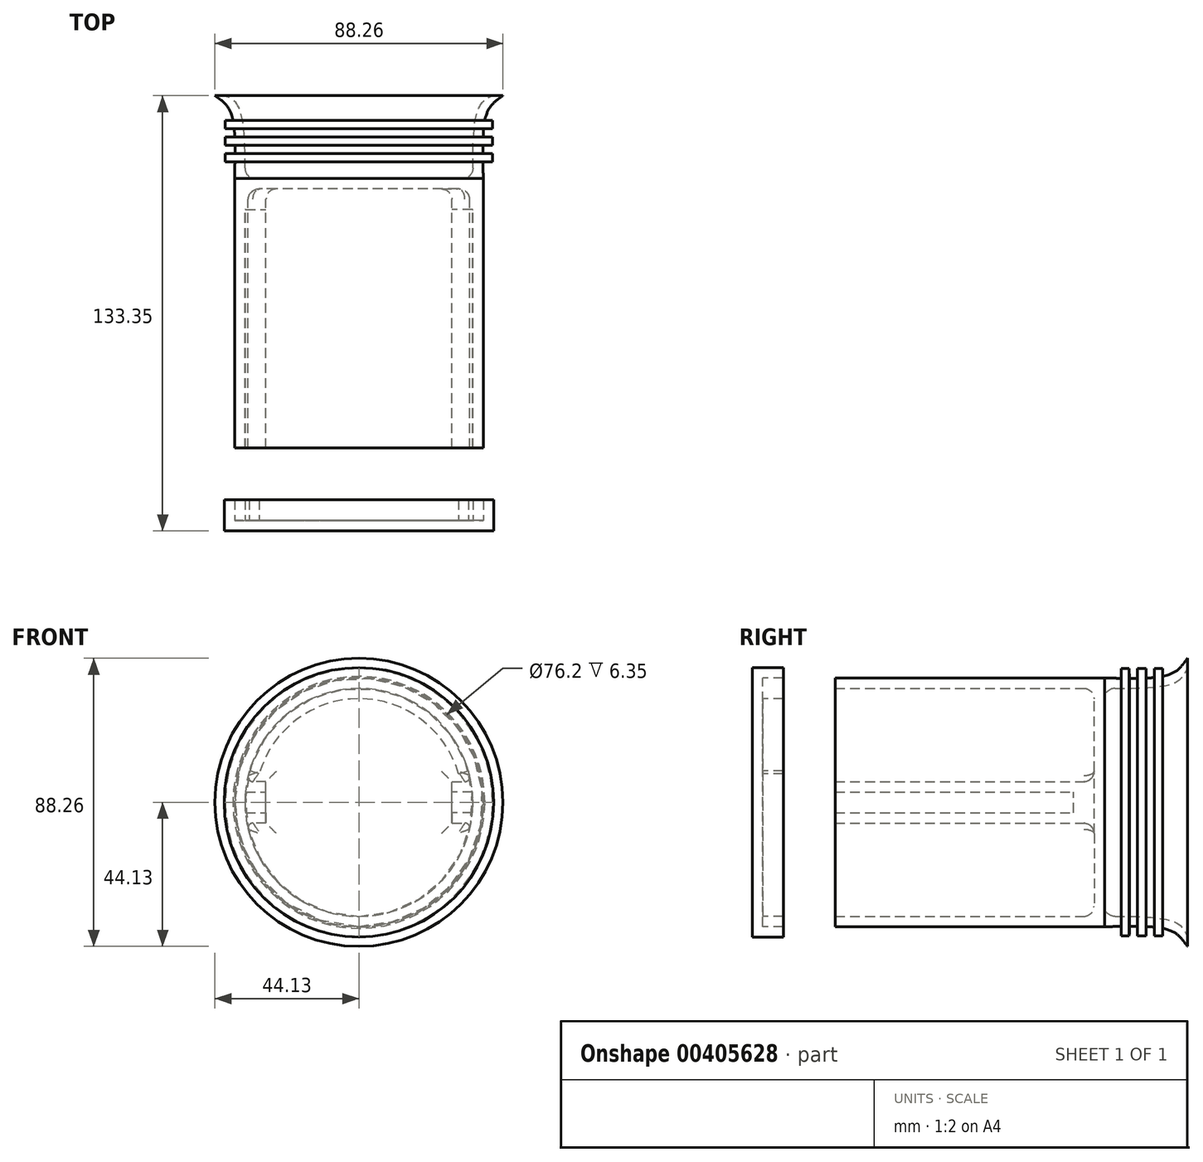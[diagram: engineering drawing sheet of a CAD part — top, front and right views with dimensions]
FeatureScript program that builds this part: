
annotation { "Feature Type Name" : "Feature", "Feature Type Description" : "" }
export const myFeature = defineFeature(function(context is Context, id is Id, definition is map)
    precondition{}
    {
        {
            var Q0;
            Q0=qCreatedBy(makeId("Front.planeOp"),FACE);
            var sketch = newSketch(context, id + "F0", { "sketchPlane" : qUnion([Q0])});
            skCircle(sketch, "E0", {"center": v(0, 0) * mm, "radius": 34.93 * mm});
            skCircle(sketch, "E1", {"center": v(0, 0) * mm, "radius": 38.1 * mm});
            skPoint(sketch, "E2", {"position": v(-38.1, 0) * mm});
            skPoint(sketch, "E3", {"position": v(38.1, 0) * mm});
            skPoint(sketch, "E4", {"position": v(-34.93, 0) * mm});
            skPoint(sketch, "E5", {"position": v(34.93, 0) * mm});
            skLineSegment(sketch, "E6", {"start": v(-38.1, 0) * mm, "end": v(38.1, 0) * mm, "construction": true});
            skLineSegment(sketch, "E7", {"start": v(34.78, -3.17) * mm, "end": v(28.48, -3.17) * mm});
            skLineSegment(sketch, "E8", {"start": v(28.48, -3.17) * mm, "end": v(28.48, -6.35) * mm});
            skLineSegment(sketch, "E9", {"start": v(28.48, -6.35) * mm, "end": v(34.34, -6.35) * mm});
            skLineSegment(sketch, "E10.MirrorCS", {"start": v(28.48, 3.17) * mm, "end": v(28.48, 6.35) * mm});
            skLineSegment(sketch, "E11.MirrorCS", {"start": v(28.48, 6.35) * mm, "end": v(34.34, 6.35) * mm});
            skLineSegment(sketch, "E12.MirrorCS", {"start": v(34.78, 3.17) * mm, "end": v(28.48, 3.17) * mm});
            skLineSegment(sketch, "E13.MirrorCS", {"start": v(-34.78, -3.17) * mm, "end": v(-28.48, -3.17) * mm});
            skLineSegment(sketch, "E14.MirrorCS", {"start": v(-28.48, 3.17) * mm, "end": v(-28.48, 6.35) * mm});
            skLineSegment(sketch, "E15.MirrorCS", {"start": v(-34.78, 3.17) * mm, "end": v(-28.48, 3.17) * mm});
            skLineSegment(sketch, "E16.MirrorCS", {"start": v(-28.48, -3.17) * mm, "end": v(-28.48, -6.35) * mm});
            skLineSegment(sketch, "E17.MirrorCS", {"start": v(-28.48, -6.35) * mm, "end": v(-34.34, -6.35) * mm});
            skLineSegment(sketch, "E18.MirrorCS", {"start": v(-28.48, 6.35) * mm, "end": v(-34.34, 6.35) * mm});
            skLineSegment(sketch, "E19", {"start": v(28.48, -3.17) * mm, "end": v(28.48, 3.17) * mm});
            skLineSegment(sketch, "E20", {"start": v(-28.48, -3.17) * mm, "end": v(-28.48, 3.17) * mm});
            skSolve(sketch);
        }
        {
            var Q0;
            Q0=makeQuery(id+"F0.imprint","IMPRINT",FACE,{"disambiguationData":[TD([[makeQuery(id+"F0.imprint","IMPRINT",EDGE,{"derivedFrom":sQuery(id+"F0.wireOp",EDGE,"E1")}),1.0]])]});
            var Q1;
            {var subQ0=sQuery(id+"F0.wireOp",EDGE,"b258979f-0020-4e8b-a2a5-557b5379ad452.MirrorCS");Q1=makeQuery(id+"F0.imprint","IMPRINT",FACE,{"disambiguationData":[TD([[makeQuery(id+"F0.imprint","IMPRINT",EDGE,{"derivedFrom":subQ0}),-1.0]])]});}
            var Q2;
            {var subQ0=sQuery(id+"F0.wireOp",EDGE,"b258979f-0020-4e8b-a2a5-557b5379ad450.MirrorCS");Q2=makeQuery(id+"F0.imprint","IMPRINT",FACE,{"disambiguationData":[TD([[makeQuery(id+"F0.imprint","IMPRINT",EDGE,{"derivedFrom":subQ0}),1.0]])]});}
            var Q3;
            {var subQ0=sQuery(id+"F0.wireOp",EDGE,"MPTAMjUX-TAAp-zu8y-YZ0W-t5zbDO9KEc0N");Q3=makeQuery(id+"F0.imprint","IMPRINT",FACE,{"disambiguationData":[TD([[makeQuery(id+"F0.imprint","IMPRINT",EDGE,{"derivedFrom":subQ0}),1.0]])]});}
            var Q4;
            {var subQ0=sQuery(id+"F0.wireOp",EDGE,"9249f0fd-918d-4ee5-9cbe-e812a7f5fd550.MirrorCS");Q4=makeQuery(id+"F0.imprint","IMPRINT",FACE,{"disambiguationData":[TD([[makeQuery(id+"F0.imprint","IMPRINT",EDGE,{"derivedFrom":subQ0}),-1.0]])]});}
            var Q5;
            {var subQ0=sQuery(id+"F0.wireOp",EDGE,"E13.MirrorCS");Q5=makeQuery(id+"F0.imprint","IMPRINT",FACE,{"disambiguationData":[TD([[makeQuery(id+"F0.imprint","IMPRINT",EDGE,{"derivedFrom":subQ0}),-1.0]])]});}
            var Q6;
            Q6=makeQuery(id+"F0.imprint","IMPRINT",FACE,{"disambiguationData":[TD([[makeQuery(id+"F0.imprint","IMPRINT",EDGE,{"derivedFrom":sQuery(id+"F0.wireOp",EDGE,"E14.MirrorCS")}),1.0]])]});
            var Q7;
            {var subQ0=sQuery(id+"F0.wireOp",EDGE,"E7");Q7=makeQuery(id+"F0.imprint","IMPRINT",FACE,{"disambiguationData":[TD([[makeQuery(id+"F0.imprint","IMPRINT",EDGE,{"derivedFrom":subQ0}),1.0]])]});}
            var Q8;
            Q8=makeQuery(id+"F0.imprint","IMPRINT",FACE,{"disambiguationData":[TD([[makeQuery(id+"F0.imprint","IMPRINT",EDGE,{"derivedFrom":sQuery(id+"F0.wireOp",EDGE,"E10.MirrorCS")}),-1.0]])]});
            extrude(context, id + "F1", {"entities" : qUnion([Q0, Q1, Q2, Q3, Q4, Q5, Q6, Q7, Q8]), "depth" : 82.55 * mm});
        }
        {
            var Q0;
            Q0=qCreatedBy(makeId("Front.planeOp"),FACE);
            cPlane(context, id + "F2", {"entities" : qUnion([Q0]), "cplaneType" : CPlaneType.OFFSET, "offset" : 107.95 * mm, "width" : 152.4 * mm, "height" : 152.4 * mm});
        }
        {
            var Q0;
            Q0=qCreatedBy(makeId("Top.planeOp"),FACE);
            var sketch = newSketch(context, id + "F3", { "sketchPlane" : qUnion([Q0])});
            skLineSegment(sketch, "E21", {"start": v(-38.1, 0) * mm, "end": v(-38.1, 25.4) * mm, "construction": true});
            skLineSegment(sketch, "E22", {"start": v(-41.53, 25.4) * mm, "end": v(-41.77, 25.4) * mm, "construction": true});
            skPoint(sketch, "E23", {"position": v(-40.96, 25.4) * mm});
            skFitSpline(sketch, "E24", {"points": [v(-38.1, 0) * mm, v(-39.35, 20.4) * mm, v(-44.13, 25.4) * mm], "startDerivative": vector(0.67, 36.34) * mm, "endDerivative": vector(-15.53, 10.92) * mm});
            skFitSpline(sketch, "E25", {"points": [v(-34.93, 0) * mm, v(-36.6, 21.36) * mm, v(-40.96, 25.4) * mm], "startDerivative": vector(0.3, 37.48) * mm, "endDerivative": vector(-17.18, 7.87) * mm});
            skLineSegment(sketch, "E26", {"start": v(-40.96, 25.4) * mm, "end": v(-40.96, 0) * mm, "construction": true});
            skLineSegment(sketch, "E27", {"start": v(-40.96, 17.78) * mm, "end": v(-38.6, 17.78) * mm});
            skLineSegment(sketch, "E28", {"start": v(-40.96, 17.78) * mm, "end": v(-40.96, 15.24) * mm});
            skLineSegment(sketch, "E29", {"start": v(-40.96, 15.24) * mm, "end": v(-38.23, 15.24) * mm});
            skLineSegment(sketch, "E30", {"start": v(-40.96, 12.7) * mm, "end": v(-38.04, 12.7) * mm});
            skLineSegment(sketch, "E31", {"start": v(-40.96, 12.7) * mm, "end": v(-40.96, 10.16) * mm});
            skLineSegment(sketch, "E32", {"start": v(-40.96, 10.16) * mm, "end": v(-37.97, 10.16) * mm});
            skLineSegment(sketch, "E33", {"start": v(-44.13, 25.4) * mm, "end": v(-40.96, 25.4) * mm});
            skLineSegment(sketch, "E34", {"start": v(0, 0) * mm, "end": v(0, 25.44) * mm, "construction": true});
            skPoint(sketch, "E35", {"position": v(-40.96, 7.62) * mm});
            skLineSegment(sketch, "E36", {"start": v(-40.96, 7.62) * mm, "end": v(-37.96, 7.66) * mm});
            skLineSegment(sketch, "E37", {"start": v(-40.96, 7.62) * mm, "end": v(-40.96, 5.08) * mm});
            skLineSegment(sketch, "E38", {"start": v(-40.96, 5.08) * mm, "end": v(-38, 5.08) * mm});
            skLineSegment(sketch, "E39", {"start": v(-38.1, 0) * mm, "end": v(-34.93, 0) * mm});
            skPoint(sketch, "E40.newPointB", {"position": v(-37.78, 25.4) * mm});
            skArc(sketch, "E40.filletArc", {"start": v(-40.4, 25.14) * mm, "mid": v(-40.95, 25.33) * mm, "end": v(-41.53, 25.4) * mm});
            skArc(sketch, "E41.filletArc", {"start": v(-41.77, 25.4) * mm, "mid": v(-42.5, 24.89) * mm, "end": v(-42.24, 24.04) * mm});
            skSolve(sketch);
        }
        {
            var Q0;
            Q0 = qSketchRegion(id + "F3", true);
            var Q1;
            Q1=sQuery(id+"F3.wireOp",EDGE,"E34");
            revolve(context, id + "F4", {"operationType" : NewBodyOperationType.ADD, "entities" : qUnion([Q0]), "axis" : qUnion([Q1]), "revolveType" : RevolveType.FULL});
        }
        {
            var Q0;
            {var subQ0=sQuery(id+"F0.wireOp",EDGE,"E7");Q0=makeQuery(id+"F0.imprint","IMPRINT",FACE,{"disambiguationData":[TD([[makeQuery(id+"F0.imprint","IMPRINT",EDGE,{"derivedFrom":subQ0}),-1.0]])]});}
            var Q1;
            {var subQ0=sQuery(id+"F0.wireOp",EDGE,"E13.MirrorCS");Q1=makeQuery(id+"F0.imprint","IMPRINT",FACE,{"disambiguationData":[TD([[makeQuery(id+"F0.imprint","IMPRINT",EDGE,{"derivedFrom":subQ0}),1.0]])]});}
            extrude(context, id + "F5", {"entities" : qUnion([Q0, Q1]), "operationType" : NewBodyOperationType.ADD, "depth" : 9.52 * mm});
        }
        {
            var Q0;
            Q0=makeQuery(id+"F0.imprint","IMPRINT",FACE,{"disambiguationData":[TD([[makeQuery(id+"F0.imprint","IMPRINT",EDGE,{"derivedFrom":sQuery(id+"F0.wireOp",EDGE,"E8")}),-1.0]])]});
            var Q1;
            Q1=makeQuery(id+"F0.imprint","IMPRINT",FACE,{"disambiguationData":[TD([[makeQuery(id+"F0.imprint","IMPRINT",EDGE,{"derivedFrom":sQuery(id+"F0.wireOp",EDGE,"E10.MirrorCS")}),-1.0]])]});
            var Q2;
            {var subQ0=sQuery(id+"F0.wireOp",EDGE,"E7");Q2=makeQuery(id+"F0.imprint","IMPRINT",FACE,{"disambiguationData":[TD([[makeQuery(id+"F0.imprint","IMPRINT",EDGE,{"derivedFrom":subQ0}),-1.0]])]});}
            var Q3;
            {var subQ0=sQuery(id+"F0.wireOp",EDGE,"E7");Q3=makeQuery(id+"F0.imprint","IMPRINT",FACE,{"disambiguationData":[TD([[makeQuery(id+"F0.imprint","IMPRINT",EDGE,{"derivedFrom":subQ0}),1.0]])]});}
            var Q4;
            Q4=makeQuery(id+"F0.imprint","IMPRINT",FACE,{"disambiguationData":[TD([[makeQuery(id+"F0.imprint","IMPRINT",EDGE,{"derivedFrom":sQuery(id+"F0.wireOp",EDGE,"E14.MirrorCS")}),1.0]])]});
            var Q5;
            {var subQ0=sQuery(id+"F0.wireOp",EDGE,"E13.MirrorCS");Q5=makeQuery(id+"F0.imprint","IMPRINT",FACE,{"disambiguationData":[TD([[makeQuery(id+"F0.imprint","IMPRINT",EDGE,{"derivedFrom":subQ0}),1.0]])]});}
            var Q6;
            {var subQ0=sQuery(id+"F0.wireOp",EDGE,"E13.MirrorCS");Q6=makeQuery(id+"F0.imprint","IMPRINT",FACE,{"disambiguationData":[TD([[makeQuery(id+"F0.imprint","IMPRINT",EDGE,{"derivedFrom":subQ0}),-1.0]])]});}
            extrude(context, id + "F6", {"entities" : qUnion([Q0, Q1, Q2, Q3, Q4, Q5, Q6]), "operationType" : NewBodyOperationType.ADD, "depth" : 3.17 * mm});
        }
        {
            var Q0;
            Q0=makeQuery(id+"F1.opExtrude","SWEPT_EDGE",EDGE,{"disambiguationData":[OSD([sQuery(id+"F0.wireOp",EDGE,"E0"),sQuery(id+"F0.wireOp",EDGE,"E17.MirrorCS")])]});
            var Q1;
            Q1=makeQuery(id+"F1.opExtrude","SWEPT_EDGE",EDGE,{"disambiguationData":[OSD([sQuery(id+"F0.wireOp",EDGE,"E0"),sQuery(id+"F0.wireOp",EDGE,"E9")])]});
            var Q2;
            Q2=makeQuery(id+"F1.opExtrude","SWEPT_EDGE",EDGE,{"disambiguationData":[OSD([sQuery(id+"F0.wireOp",EDGE,"E0"),sQuery(id+"F0.wireOp",EDGE,"E11.MirrorCS")])]});
            var Q3;
            Q3=makeQuery(id+"F1.opExtrude","SWEPT_EDGE",EDGE,{"disambiguationData":[OSD([sQuery(id+"F0.wireOp",EDGE,"E0"),sQuery(id+"F0.wireOp",EDGE,"E18.MirrorCS")])]});
            fillet(context, id + "F7", {"entities" : qUnion([Q0, Q1, Q2, Q3]), "radius" : 1.52 * mm, "tangentPropagation" : true, "allowEdgeOverflow" : false});
        }
        {
            var Q0;
            Q0=qCreatedBy(id+"F2.planeOp",FACE);
            var sketch = newSketch(context, id + "F8", { "sketchPlane" : qUnion([Q0])});
            skPoint(sketch, "E42", {"position": v(-38.1, 0) * mm});
            skPoint(sketch, "E43", {"position": v(-34.92, 0) * mm});
            skPoint(sketch, "E44", {"position": v(34.93, 0) * mm});
            skPoint(sketch, "E45", {"position": v(38.1, 0) * mm});
            skCircle(sketch, "E46", {"center": v(0, 0) * mm, "radius": 38.1 * mm});
            skCircle(sketch, "E47", {"center": v(0, 0) * mm, "radius": 41.28 * mm});
            skArc(sketch, "E48", {"start": v(-33.57, 9.63) * mm, "mid": v(0, 34.92) * mm, "end": v(33.57, 9.63) * mm});
            skLineSegment(sketch, "E49", {"start": v(-33.57, 9.63) * mm, "end": v(0, 0) * mm, "construction": true});
            skLineSegment(sketch, "E50", {"start": v(0, 0) * mm, "end": v(33.57, 9.63) * mm, "construction": true});
            skArc(sketch, "E51", {"start": v(-30.52, 8.75) * mm, "mid": v(0, 31.75) * mm, "end": v(30.52, 8.75) * mm});
            skLineSegment(sketch, "E52", {"start": v(-30.52, 8.75) * mm, "end": v(-33.57, 9.63) * mm});
            skLineSegment(sketch, "E53", {"start": v(30.52, 8.75) * mm, "end": v(33.57, 9.63) * mm});
            skLineSegment(sketch, "E54.MirrorCS", {"start": v(0, 0) * mm, "end": v(33.57, -9.63) * mm, "construction": true});
            skArc(sketch, "E55.MirrorCS", {"start": v(-30.52, -8.75) * mm, "mid": v(0, -31.75) * mm, "end": v(30.52, -8.75) * mm});
            skArc(sketch, "E56.MirrorCS", {"start": v(-33.57, -9.63) * mm, "mid": v(0, -34.92) * mm, "end": v(33.57, -9.63) * mm});
            skLineSegment(sketch, "E57.MirrorCS", {"start": v(-33.57, -9.63) * mm, "end": v(0, 0) * mm, "construction": true});
            skLineSegment(sketch, "E58", {"start": v(-30.52, -8.75) * mm, "end": v(-33.57, -9.63) * mm});
            skLineSegment(sketch, "E59", {"start": v(30.52, -8.75) * mm, "end": v(33.57, -9.63) * mm});
            skCircle(sketch, "E60", {"center": v(0, 0) * mm, "radius": 34.92 * mm});
            skSolve(sketch);
        }
        {
            var Q0;
            Q0 = qSketchRegion(id + "F8", true);
            var Q1;
            Q1=makeQuery(id+"F8.imprint","IMPRINT",FACE,{"disambiguationData":[TD([[makeQuery(id+"F8.imprint","IMPRINT",EDGE,{"derivedFrom":sQuery(id+"F8.wireOp",EDGE,"E46")}),1.0]])]});
            var Q2;
            Q2=makeQuery(id+"F8.imprint","IMPRINT",FACE,{"disambiguationData":[TD([[makeQuery(id+"F8.imprint","IMPRINT",EDGE,{"derivedFrom":sQuery(id+"F8.wireOp",EDGE,"E51")}),1.0]])]});
            var Q3;
            Q3=makeQuery(id+"F8.imprint","IMPRINT",FACE,{"disambiguationData":[TD([[makeQuery(id+"F8.imprint","IMPRINT",EDGE,{"derivedFrom":sQuery(id+"F8.wireOp",EDGE,"E55.MirrorCS")}),-1.0]])]});
            var Q4;
            Q4=makeQuery(id+"F8.imprint","IMPRINT",FACE,{"disambiguationData":[TD([[makeQuery(id+"F8.imprint","IMPRINT",EDGE,{"derivedFrom":sQuery(id+"F8.wireOp",EDGE,"E51")}),-1.0]])]});
            extrude(context, id + "F9", {"entities" : qUnion([Q0, Q1, Q2, Q3, Q4]), "oppositeDirection" : true, "depth" : 3.17 * mm});
        }
        {
            var Q0;
            Q0=makeQuery(id+"F8.imprint","IMPRINT",FACE,{"disambiguationData":[TD([[makeQuery(id+"F8.imprint","IMPRINT",EDGE,{"derivedFrom":sQuery(id+"F8.wireOp",EDGE,"E46")}),-1.0]])]});
            var Q1;
            Q1=makeQuery(id+"F8.imprint","IMPRINT",FACE,{"disambiguationData":[TD([[makeQuery(id+"F8.imprint","IMPRINT",EDGE,{"derivedFrom":sQuery(id+"F8.wireOp",EDGE,"E51")}),1.0]])]});
            var Q2;
            Q2=makeQuery(id+"F8.imprint","IMPRINT",FACE,{"disambiguationData":[TD([[makeQuery(id+"F8.imprint","IMPRINT",EDGE,{"derivedFrom":sQuery(id+"F8.wireOp",EDGE,"E55.MirrorCS")}),-1.0]])]});
            extrude(context, id + "F10", {"entities" : qUnion([Q0, Q1, Q2]), "operationType" : NewBodyOperationType.ADD, "oppositeDirection" : true, "depth" : 9.52 * mm});
        }
        {
            var Q0;
            Q0=makeQuery(id+"F6.opExtrude","CAP_FACE",FACE,{"disambiguationData":[OSD([sQuery(id+"F0.wireOp",EDGE,"E0")])],"isStart":false});
            var Q1;
            {var subQ0=sQuery(id+"F0.wireOp",EDGE,"E0");var subQ1=sQuery(id+"F0.wireOp",EDGE,"E15.MirrorCS");var subQ2=sQuery(id+"F0.wireOp",EDGE,"E13.MirrorCS");var subQ3=sQuery(id+"F0.wireOp",EDGE,"E14.MirrorCS");var subQ5=sQuery(id+"F0.wireOp",EDGE,"E11.MirrorCS");var subQ6=sQuery(id+"F0.wireOp",EDGE,"E18.MirrorCS");var subQ9=sQuery(id+"F0.wireOp",EDGE,"E17.MirrorCS");var subQ10=sQuery(id+"F0.wireOp",EDGE,"E16.MirrorCS");var subQ11=sQuery(id+"F0.wireOp",EDGE,"E12.MirrorCS");var subQ12=sQuery(id+"F0.wireOp",EDGE,"E10.MirrorCS");var subQ13=sQuery(id+"F0.wireOp",EDGE,"E9");var subQ14=sQuery(id+"F0.wireOp",EDGE,"E8");var subQ15=sQuery(id+"F0.wireOp",EDGE,"E7");var subQ16=makeQuery(id+"F1.opExtrude","CAP_FACE",FACE,{"disambiguationData":[OSD([subQ0,sQuery(id+"F0.wireOp",EDGE,"E1"),subQ15,subQ14,subQ13,subQ12,subQ5,subQ11,subQ2,subQ3,subQ1,subQ10,subQ9,subQ6])],"isStart":true});Q1=makeQuery(id+"F6.boolean.opBoolean","MERGE",FACE,{"derivedFrom":[makeQuery(id+"F5.boolean.opBoolean","MERGE",FACE,{"derivedFrom":[makeQuery(id+"F4.boolean.opBoolean","SPLIT",FACE,{"disambiguationData":[TD([makeQuery(id+"F1.opExtrude","SWEPT_FACE",FACE,{"disambiguationData":[OSD([subQ15])]})])],"derivedFrom":subQ16}),makeQuery(id+"F4.boolean.opBoolean","SPLIT",FACE,{"disambiguationData":[TD([makeQuery(id+"F1.opExtrude","SWEPT_FACE",FACE,{"disambiguationData":[OSD([subQ12])]})])],"derivedFrom":subQ16}),makeQuery(id+"F5.opExtrude","CAP_FACE",FACE,{"disambiguationData":[OSD([subQ0,subQ15,subQ11,sQuery(id+"F0.wireOp",EDGE,"E19")])],"isStart":true})]}),makeQuery(id+"F5.boolean.opBoolean","MERGE",FACE,{"derivedFrom":[makeQuery(id+"F4.boolean.opBoolean","SPLIT",FACE,{"disambiguationData":[TD([makeQuery(id+"F1.opExtrude","SWEPT_FACE",FACE,{"disambiguationData":[OSD([subQ2])]})])],"derivedFrom":subQ16}),makeQuery(id+"F4.boolean.opBoolean","SPLIT",FACE,{"disambiguationData":[TD([makeQuery(id+"F1.opExtrude","SWEPT_FACE",FACE,{"disambiguationData":[OSD([subQ3])]})])],"derivedFrom":subQ16}),makeQuery(id+"F5.opExtrude","CAP_FACE",FACE,{"disambiguationData":[OSD([subQ0,subQ2,subQ1,sQuery(id+"F0.wireOp",EDGE,"E20")])],"isStart":true})]}),makeQuery(id+"F6.opExtrude","CAP_FACE",FACE,{"disambiguationData":[OSD([subQ0])],"isStart":true})]});}
            fillet(context, id + "F11", {"entities" : qUnion([Q0, Q1]), "radius" : 3.17 * mm, "tangentPropagation" : true, "allowEdgeOverflow" : false});
        }
    });
